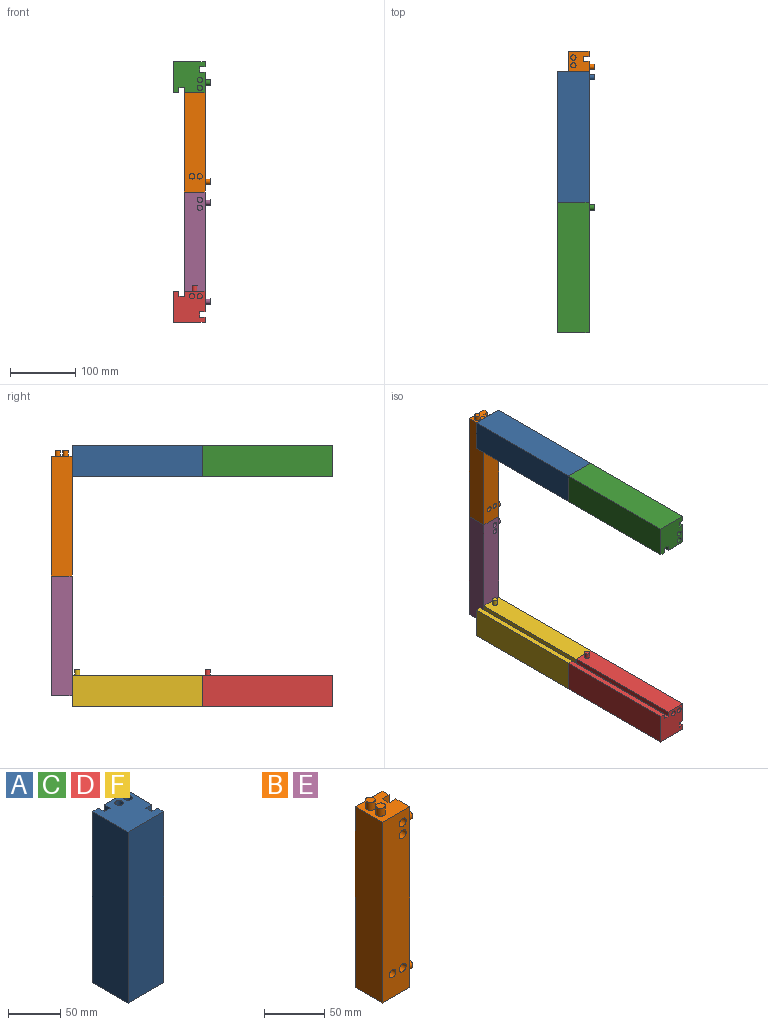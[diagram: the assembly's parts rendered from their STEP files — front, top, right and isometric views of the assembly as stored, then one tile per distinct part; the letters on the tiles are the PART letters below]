
ASSEMBLY  parts=6 mates=5
PART A: 24 faces, bbox 48x56x208 mm
  f0: plane 200x8mm, normal (0,1,0), area 1600mm2, adj f1,f11,f12,f13
  f1: plane 200x8mm, normal (1,0,0), area 1600mm2, adj f0,f2,f12,f13
  f2: plane 200x8mm, normal (0,1,0), area 1600mm2, adj f1,f3,f12,f13
  f3: plane 200x48mm, normal (-1,0,0), area 9600mm2, adj f2,f4,f12,f13
  f4: plane 200x48mm, normal (0,-1,0), area 9600mm2, adj f3,f5,f12,f13
  f5: plane 200x8mm, normal (1,0,0), area 1600mm2, adj f4,f6,f12,f13
  f6: plane 200x8mm, normal (0,1,0), area 1600mm2, adj f5,f7,f12,f13
  f7: plane 200x8mm, normal (1,0,0), area 1600mm2, adj f6,f8,f12,f13
  f8: plane 200x8mm, normal (0,-1,0), area 1600mm2, adj f7,f9,f12,f13
  f9: plane 200x32mm, normal (1,0,0), area 6400mm2, adj f8,f10,f12,f13
  f10: plane 200x32mm, normal (0,1,0), area 6349.7mm2, adj f9,f11,f12,f13,f22
  f11: plane 200x8mm, normal (-1,0,0), area 1600mm2, adj f0,f10,f12,f13
  f12: plane 48x48mm, normal (0,0,1), area 2072.9mm2, adj f0,f1,f2,f3,f4,f5,f6,f7
  f13: plane 48x48mm, normal (0,0,-1), area 2075.5mm2, adj f0,f1,f2,f3,f4,f5,f6,f7
  f14: cylinder r=4mm len=8mm, axis (0,0,1), area 201.1mm2, adj f13,f15
  f15: plane 8x8mm, normal (0,0,-1), area 50.3mm2, adj f14
  f16: cylinder r=4mm len=8mm, axis (0,0,1), area 201.1mm2, adj f13,f17
  f17: plane 8x8mm, normal (0,0,-1), area 50.3mm2, adj f16
  f18: cylinder r=4.05mm len=8.1mm, axis (0,0,1), area 206.1mm2, adj f12,f19
  f19: plane 8.1x8.1mm, normal (0,0,1), area 51.5mm2, adj f18
  f20: cylinder r=4.05mm len=8.1mm, axis (0,0,1), area 206.1mm2, adj f12,f21
  f21: plane 8.1x8.1mm, normal (0,0,1), area 51.5mm2, adj f20
  f22: cylinder r=4mm len=8mm, axis (0,-1,0), area 201.1mm2, adj f10,f23
  f23: plane 8x8mm, normal (0,1,0), area 50.3mm2, adj f22
PART B: 30 faces, bbox 40x32x192 mm
  f0: plane 184x32mm, normal (0,1,0), area 5888mm2, adj f1,f7,f8,f9
  f1: plane 184x32mm, normal (-1,0,0), area 5888mm2, adj f0,f2,f8,f9
  f2: plane 184x32mm, normal (0,-1,0), area 5681.9mm2, adj f1,f3,f8,f9,f10,f12,f14,f16
  f3: plane 184x16mm, normal (1,0,0), area 2843.5mm2, adj f2,f4,f8,f9,f26,f28
  f4: plane 184x8mm, normal (0,1,0), area 1472mm2, adj f3,f5,f8,f9
  f5: plane 184x8mm, normal (1,0,0), area 1472mm2, adj f4,f6,f8,f9
  f6: plane 184x8mm, normal (0,-1,0), area 1472mm2, adj f5,f7,f8,f9
  f7: plane 184x8mm, normal (1,0,0), area 1472mm2, adj f0,f6,f8,f9
  f8: plane 32x32mm, normal (0,0,1), area 859.5mm2, adj f0,f1,f2,f3,f4,f5,f6,f7
  f9: plane 32x32mm, normal (0,0,-1), area 856.9mm2, adj f0,f1,f2,f3,f4,f5,f6,f7
  f10: cylinder r=4.05mm len=8.1mm, axis (0,-1,0), area 206.1mm2, adj f2,f11
  f11: plane 8.1x8.1mm, normal (0,-1,0), area 51.5mm2, adj f10
  f12: cylinder r=4.05mm len=8.1mm, axis (0,-1,0), area 206.1mm2, adj f2,f13
  f13: plane 8.1x8.1mm, normal (0,-1,0), area 51.5mm2, adj f12
  f14: cylinder r=4.05mm len=8.1mm, axis (0,-1,0), area 206.1mm2, adj f2,f15
  f15: plane 8.1x8.1mm, normal (0,-1,0), area 51.5mm2, adj f14
  f16: cylinder r=4.05mm len=8.1mm, axis (0,-1,0), area 206.1mm2, adj f2,f17
  f17: plane 8.1x8.1mm, normal (0,-1,0), area 51.5mm2, adj f16
  f18: cylinder r=4mm len=8mm, axis (0,0,-1), area 201.1mm2, adj f8,f19
  f19: plane 8x8mm, normal (0,0,1), area 50.3mm2, adj f18
  f20: cylinder r=4mm len=8mm, axis (0,0,-1), area 201.1mm2, adj f8,f21
  f21: plane 8x8mm, normal (0,0,1), area 50.3mm2, adj f20
  f22: cylinder r=4.05mm len=8.1mm, axis (0,0,-1), area 206.1mm2, adj f9,f23
  f23: plane 8.1x8.1mm, normal (0,0,-1), area 51.5mm2, adj f22
  f24: cylinder r=4.05mm len=8.1mm, axis (0,0,-1), area 206.1mm2, adj f9,f25
  f25: plane 8.1x8.1mm, normal (0,0,-1), area 51.5mm2, adj f24
  f26: cylinder r=4mm len=8mm, axis (-1,0,0), area 201.1mm2, adj f3,f27
  f27: plane 8x8mm, normal (1,0,0), area 50.3mm2, adj f26
  f28: cylinder r=4mm len=8mm, axis (-1,0,0), area 201.1mm2, adj f3,f29
  f29: plane 8x8mm, normal (1,0,0), area 50.3mm2, adj f28
PART C: same geometry as A
PART D: same geometry as A
PART E: same geometry as B
PART F: same geometry as A
PLACE A rot(axis=(0.58,0.58,-0.58),120deg) t=(109.54,-264.85,215.63)mm
PLACE B t=(117.54,-148.85,131.63)mm
PLACE C rot(axis=(0.58,0.58,-0.58),120deg) t=(109.54,-464.85,215.63)mm
PLACE D rot(axis=(1,0,0),90deg) t=(109.54,-464.85,-136.37)mm
PLACE E t=(117.54,-148.85,-52.37)mm
PLACE F rot(axis=(1,0,0),90deg) t=(109.54,-264.85,-136.37)mm
MATE fastened B.f20 <-> E.f20  axis (0,0,-1) through (109.54,-142.85,39.63)mm
MATE fastened A.f14 <-> B.f10  axis (0,-1,0) through (125.54,-164.85,199.63)mm
MATE fastened D.f16 <-> F.f16  axis (0,1,0) through (113.54,-364.85,-120.37)mm
MATE fastened C.f16 <-> A.f16  axis (0,1,0) through (125.54,-364.85,211.63)mm
MATE fastened E.f12 <-> F.f16  axis (0,-1,0) through (113.54,-164.85,-120.37)mm
